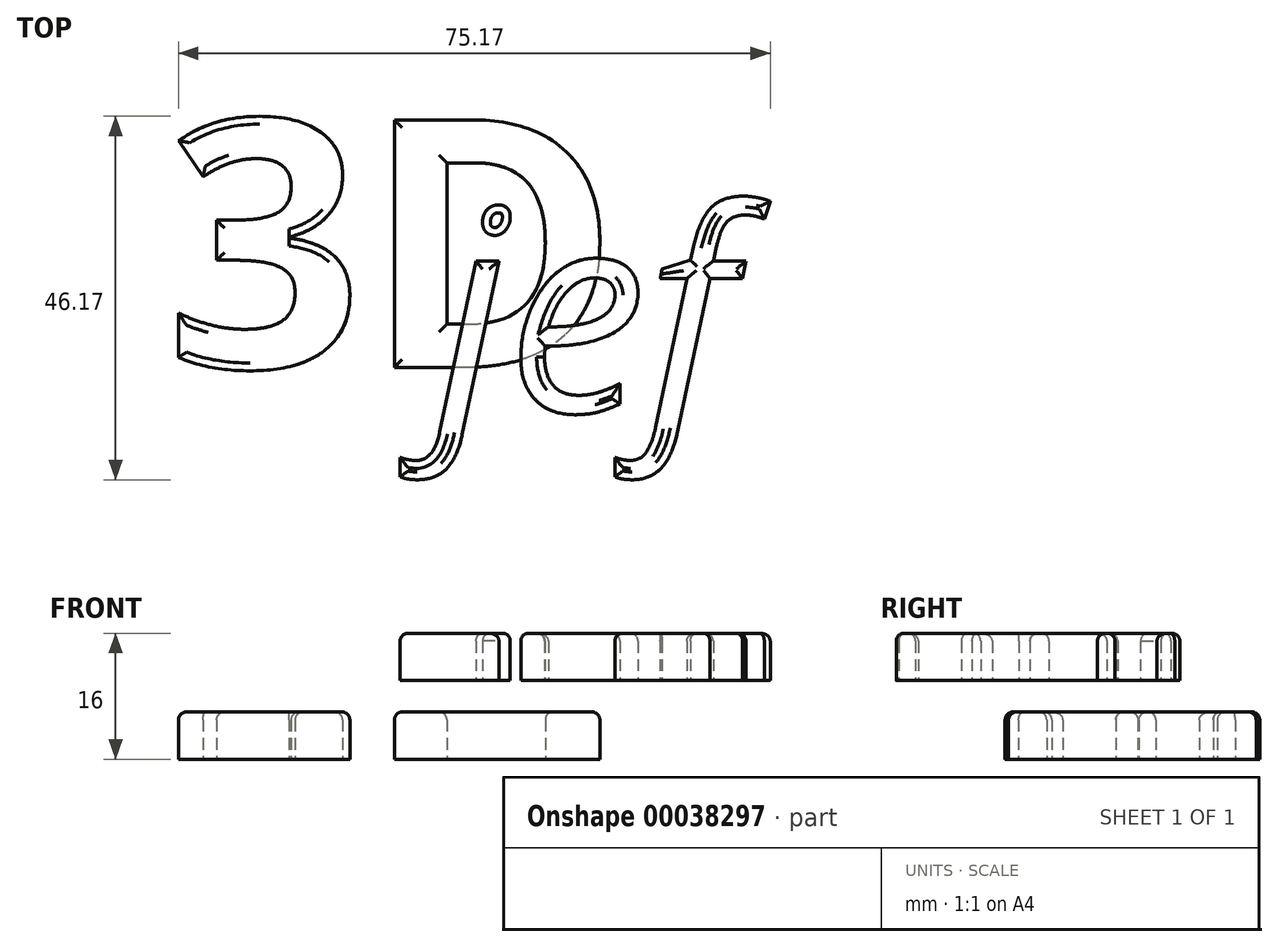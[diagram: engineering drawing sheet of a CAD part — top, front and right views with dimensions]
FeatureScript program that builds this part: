
annotation { "Feature Type Name" : "Feature", "Feature Type Description" : "" }
export const myFeature = defineFeature(function(context is Context, id is Id, definition is map)
    precondition{}
    {
        {
            var Q0;
            Q0=qCreatedBy(makeId("Top.planeOp"),FACE);
            var sketch = newSketch(context, id + "F0", { "sketchPlane" : qUnion([Q0])});
            skText(sketch, "E0", { "text": "3D", "fontName": "OpenSans-Bold.ttf"});
            const initialGuessF0  = {"E0": [-0.0552, 0, 1, 0, 0.03172]};
            skSetInitialGuess(sketch, initialGuessF0);
            skSolve(sketch);
        }
        {
            var Q0;
            Q0=makeQuery(id+"F0.imprint","IMPRINT",FACE,{"disambiguationData":[TD([[makeQuery(id+"F0.imprint","IMPRINT",EDGE,{"derivedFrom":sQuery(id+"F0.wireOp",EDGE,"E0.sketch_text.stroke-0")}),-1.0]])]});
            var Q1;
            Q1=makeQuery(id+"F0.imprint","IMPRINT",FACE,{"disambiguationData":[TD([[makeQuery(id+"F0.imprint","IMPRINT",EDGE,{"derivedFrom":sQuery(id+"F0.wireOp",EDGE,"1949aad5-839d-4fb3-a845-ca18cb88f10a.sketch_text.stroke-0")}),-1.0]])]});
            var Q2;
            Q2=makeQuery(id+"F0.imprint","IMPRINT",FACE,{"disambiguationData":[TD([[makeQuery(id+"F0.imprint","IMPRINT",EDGE,{"derivedFrom":sQuery(id+"F0.wireOp",EDGE,"1949aad5-839d-4fb3-a845-ca18cb88f10a.sketch_text.stroke-9")}),-1.0]])]});
            var Q3;
            Q3=makeQuery(id+"F0.imprint","IMPRINT",FACE,{"disambiguationData":[TD([[makeQuery(id+"F0.imprint","IMPRINT",EDGE,{"derivedFrom":sQuery(id+"F0.wireOp",EDGE,"1949aad5-839d-4fb3-a845-ca18cb88f10a.sketch_text.stroke-41")}),-1.0]])]});
            var Q4;
            Q4=makeQuery(id+"F0.imprint","IMPRINT",FACE,{"disambiguationData":[TD([[makeQuery(id+"F0.imprint","IMPRINT",EDGE,{"derivedFrom":sQuery(id+"F0.wireOp",EDGE,"E0.sketch_text.stroke-27")}),-1.0]])]});
            var Q5;
            Q5=makeQuery(id+"F0.imprint","IMPRINT",FACE,{"disambiguationData":[TD([[makeQuery(id+"F0.imprint","IMPRINT",EDGE,{"derivedFrom":sQuery(id+"F0.wireOp",EDGE,"1949aad5-839d-4fb3-a845-ca18cb88f10a.sketch_text.stroke-16")}),-1.0]])]});
            extrude(context, id + "F1", {"entities" : qUnion([Q0, Q1, Q2, Q3, Q4, Q5]), "depth" : 6 * mm});
        }
        {
            var Q0;
            Q0=makeQuery(id+"F1.opExtrude","CAP_EDGE",EDGE,{"disambiguationData":[OSD([sQuery(id+"F0.wireOp",EDGE,"E0.sketch_text.stroke-6")])],"isStart":false});
            var Q1;
            Q1=makeQuery(id+"F1.opExtrude","CAP_EDGE",EDGE,{"disambiguationData":[OSD([sQuery(id+"F0.wireOp",EDGE,"E0.sketch_text.stroke-0")])],"isStart":false});
            var Q2;
            Q2=makeQuery(id+"F1.opExtrude","CAP_EDGE",EDGE,{"disambiguationData":[OSD([sQuery(id+"F0.wireOp",EDGE,"E0.sketch_text.stroke-23")])],"isStart":false});
            var Q3;
            Q3=makeQuery(id+"F1.opExtrude","CAP_EDGE",EDGE,{"disambiguationData":[OSD([sQuery(id+"F0.wireOp",EDGE,"E0.sketch_text.stroke-21")])],"isStart":false});
            var Q4;
            Q4=makeQuery(id+"F1.opExtrude","CAP_EDGE",EDGE,{"disambiguationData":[OSD([sQuery(id+"F0.wireOp",EDGE,"E0.sketch_text.stroke-16")])],"isStart":false});
            var Q5;
            Q5=makeQuery(id+"F1.opExtrude","CAP_EDGE",EDGE,{"disambiguationData":[OSD([sQuery(id+"F0.wireOp",EDGE,"E0.sketch_text.stroke-14")])],"isStart":false});
            var Q6;
            Q6=makeQuery(id+"F1.opExtrude","CAP_EDGE",EDGE,{"disambiguationData":[OSD([sQuery(id+"F0.wireOp",EDGE,"E0.sketch_text.stroke-8")])],"isStart":false});
            var Q7;
            Q7=makeQuery(id+"F1.opExtrude","CAP_EDGE",EDGE,{"disambiguationData":[OSD([sQuery(id+"F0.wireOp",EDGE,"E0.sketch_text.stroke-30")])],"isStart":false});
            var Q8;
            Q8=makeQuery(id+"F1.opExtrude","CAP_EDGE",EDGE,{"disambiguationData":[OSD([sQuery(id+"F0.wireOp",EDGE,"E0.sketch_text.stroke-31")])],"isStart":false});
            var Q9;
            Q9=makeQuery(id+"F1.opExtrude","CAP_EDGE",EDGE,{"disambiguationData":[OSD([sQuery(id+"F0.wireOp",EDGE,"E0.sketch_text.stroke-36")])],"isStart":false});
            var Q10;
            Q10=makeQuery(id+"F1.opExtrude","CAP_EDGE",EDGE,{"disambiguationData":[OSD([sQuery(id+"F0.wireOp",EDGE,"E0.sketch_text.stroke-35")])],"isStart":false});
            fillet(context, id + "F2", {"entities" : qUnion([Q0, Q1, Q2, Q3, Q4, Q5, Q6, Q7, Q8, Q9, Q10]), "radius" : 1 * mm, "tangentPropagation" : true, "allowEdgeOverflow" : false});
        }
        {
            var Q0;
            Q0=qCreatedBy(makeId("Top.planeOp"),FACE);
            cPlane(context, id + "F3", {"entities" : qUnion([Q0]), "cplaneType" : CPlaneType.OFFSET, "offset" : 10 * mm, "width" : 150 * mm, "height" : 150 * mm});
        }
        {
            var Q0;
            Q0=qCreatedBy(id+"F3.planeOp",FACE);
            var sketch = newSketch(context, id + "F4", { "sketchPlane" : qUnion([Q0])});
            skText(sketch, "E1", { "text": "jef", "fontName": "OpenSans-Italic.ttf"});
            const initialGuessF4  = {"E1": [-0.02085, -0.00566, 1, 0, 0.0258]};
            skSetInitialGuess(sketch, initialGuessF4);
            skSolve(sketch);
        }
        {
            var Q0;
            Q0 = qSketchRegion(id + "F4", true);
            extrude(context, id + "F5", {"entities" : qUnion([Q0]), "depth" : 6 * mm});
        }
        {
            var Q0;
            Q0=makeQuery(id+"F5.opExtrude","CAP_FACE",FACE,{"disambiguationData":[OSD([sQuery(id+"F4.wireOp",EDGE,"E1.sketch_text.stroke-0"),sQuery(id+"F4.wireOp",EDGE,"E1.sketch_text.stroke-1"),sQuery(id+"F4.wireOp",EDGE,"E1.sketch_text.stroke-2"),sQuery(id+"F4.wireOp",EDGE,"E1.sketch_text.stroke-3"),sQuery(id+"F4.wireOp",EDGE,"E1.sketch_text.stroke-4"),sQuery(id+"F4.wireOp",EDGE,"E1.sketch_text.stroke-5"),sQuery(id+"F4.wireOp",EDGE,"E1.sketch_text.stroke-6"),sQuery(id+"F4.wireOp",EDGE,"E1.sketch_text.stroke-7"),sQuery(id+"F4.wireOp",EDGE,"E1.sketch_text.stroke-8")])],"isStart":false});
            var Q1;
            Q1=makeQuery(id+"F5.opExtrude","CAP_FACE",FACE,{"disambiguationData":[OSD([sQuery(id+"F4.wireOp",EDGE,"E1.sketch_text.stroke-9"),sQuery(id+"F4.wireOp",EDGE,"E1.sketch_text.stroke-10"),sQuery(id+"F4.wireOp",EDGE,"E1.sketch_text.stroke-11"),sQuery(id+"F4.wireOp",EDGE,"E1.sketch_text.stroke-12"),sQuery(id+"F4.wireOp",EDGE,"E1.sketch_text.stroke-13"),sQuery(id+"F4.wireOp",EDGE,"E1.sketch_text.stroke-14"),sQuery(id+"F4.wireOp",EDGE,"E1.sketch_text.stroke-15")])],"isStart":false});
            var Q2;
            Q2=makeQuery(id+"F5.opExtrude","CAP_FACE",FACE,{"disambiguationData":[OSD([sQuery(id+"F4.wireOp",EDGE,"E1.sketch_text.stroke-16"),sQuery(id+"F4.wireOp",EDGE,"E1.sketch_text.stroke-17"),sQuery(id+"F4.wireOp",EDGE,"E1.sketch_text.stroke-18"),sQuery(id+"F4.wireOp",EDGE,"E1.sketch_text.stroke-19"),sQuery(id+"F4.wireOp",EDGE,"E1.sketch_text.stroke-20"),sQuery(id+"F4.wireOp",EDGE,"E1.sketch_text.stroke-21"),sQuery(id+"F4.wireOp",EDGE,"E1.sketch_text.stroke-22"),sQuery(id+"F4.wireOp",EDGE,"E1.sketch_text.stroke-23"),sQuery(id+"F4.wireOp",EDGE,"E1.sketch_text.stroke-24"),sQuery(id+"F4.wireOp",EDGE,"E1.sketch_text.stroke-25"),sQuery(id+"F4.wireOp",EDGE,"E1.sketch_text.stroke-26"),sQuery(id+"F4.wireOp",EDGE,"E1.sketch_text.stroke-27"),sQuery(id+"F4.wireOp",EDGE,"E1.sketch_text.stroke-28"),sQuery(id+"F4.wireOp",EDGE,"E1.sketch_text.stroke-29"),sQuery(id+"F4.wireOp",EDGE,"E1.sketch_text.stroke-30"),sQuery(id+"F4.wireOp",EDGE,"E1.sketch_text.stroke-31"),sQuery(id+"F4.wireOp",EDGE,"E1.sketch_text.stroke-32"),sQuery(id+"F4.wireOp",EDGE,"E1.sketch_text.stroke-33"),sQuery(id+"F4.wireOp",EDGE,"E1.sketch_text.stroke-34"),sQuery(id+"F4.wireOp",EDGE,"E1.sketch_text.stroke-35"),sQuery(id+"F4.wireOp",EDGE,"E1.sketch_text.stroke-36"),sQuery(id+"F4.wireOp",EDGE,"E1.sketch_text.stroke-37"),sQuery(id+"F4.wireOp",EDGE,"E1.sketch_text.stroke-38"),sQuery(id+"F4.wireOp",EDGE,"E1.sketch_text.stroke-39"),sQuery(id+"F4.wireOp",EDGE,"E1.sketch_text.stroke-40")])],"isStart":false});
            var Q3;
            Q3=makeQuery(id+"F5.opExtrude","CAP_FACE",FACE,{"disambiguationData":[OSD([sQuery(id+"F4.wireOp",EDGE,"E1.sketch_text.stroke-41"),sQuery(id+"F4.wireOp",EDGE,"E1.sketch_text.stroke-42"),sQuery(id+"F4.wireOp",EDGE,"E1.sketch_text.stroke-43"),sQuery(id+"F4.wireOp",EDGE,"E1.sketch_text.stroke-44"),sQuery(id+"F4.wireOp",EDGE,"E1.sketch_text.stroke-45"),sQuery(id+"F4.wireOp",EDGE,"E1.sketch_text.stroke-46"),sQuery(id+"F4.wireOp",EDGE,"E1.sketch_text.stroke-47"),sQuery(id+"F4.wireOp",EDGE,"E1.sketch_text.stroke-48"),sQuery(id+"F4.wireOp",EDGE,"E1.sketch_text.stroke-49"),sQuery(id+"F4.wireOp",EDGE,"E1.sketch_text.stroke-50"),sQuery(id+"F4.wireOp",EDGE,"E1.sketch_text.stroke-51"),sQuery(id+"F4.wireOp",EDGE,"E1.sketch_text.stroke-52"),sQuery(id+"F4.wireOp",EDGE,"E1.sketch_text.stroke-53"),sQuery(id+"F4.wireOp",EDGE,"E1.sketch_text.stroke-54"),sQuery(id+"F4.wireOp",EDGE,"E1.sketch_text.stroke-55"),sQuery(id+"F4.wireOp",EDGE,"E1.sketch_text.stroke-56"),sQuery(id+"F4.wireOp",EDGE,"E1.sketch_text.stroke-57"),sQuery(id+"F4.wireOp",EDGE,"E1.sketch_text.stroke-58"),sQuery(id+"F4.wireOp",EDGE,"E1.sketch_text.stroke-59"),sQuery(id+"F4.wireOp",EDGE,"E1.sketch_text.stroke-60"),sQuery(id+"F4.wireOp",EDGE,"E1.sketch_text.stroke-61"),sQuery(id+"F4.wireOp",EDGE,"E1.sketch_text.stroke-62"),sQuery(id+"F4.wireOp",EDGE,"E1.sketch_text.stroke-63"),sQuery(id+"F4.wireOp",EDGE,"E1.sketch_text.stroke-64"),sQuery(id+"F4.wireOp",EDGE,"E1.sketch_text.stroke-65")])],"isStart":false});
            fillet(context, id + "F6", {"entities" : qUnion([Q0, Q1, Q2, Q3]), "radius" : 1 * mm, "tangentPropagation" : true, "allowEdgeOverflow" : false});
        }
    });
